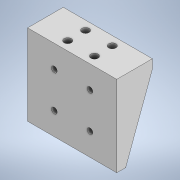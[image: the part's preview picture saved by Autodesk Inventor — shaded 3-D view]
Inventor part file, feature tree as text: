
AUTODESK INVENTOR PART (.ipt)
format: ipt  version: 2021 (Build 250183000, 183)  size: 144,384 bytes
history: native  units: mm
features: sketch x3, hole x2, other x1, extrude x1
ambient origin geometry x8: Origin, YZ Plane, XZ Plane, XY Plane, X Axis, Y Axis, Z Axis, Center Point
bodies: Body1 (feature_tree)
feature tree (7):
  other  "實體1"
  extrude  "擠出1"  Depth=45.4mm
  hole  "孔1"  [1 undecoded]
  hole  "孔2"  [1 undecoded]
  sketch  "草圖1"
  sketch  "草圖2"
  sketch  "草圖3"
note: 2 required parameter values undecoded (feature->parameter linkage not recoverable at this tier; creation-order binding heuristic only, values carry confidence <= 0.55)
